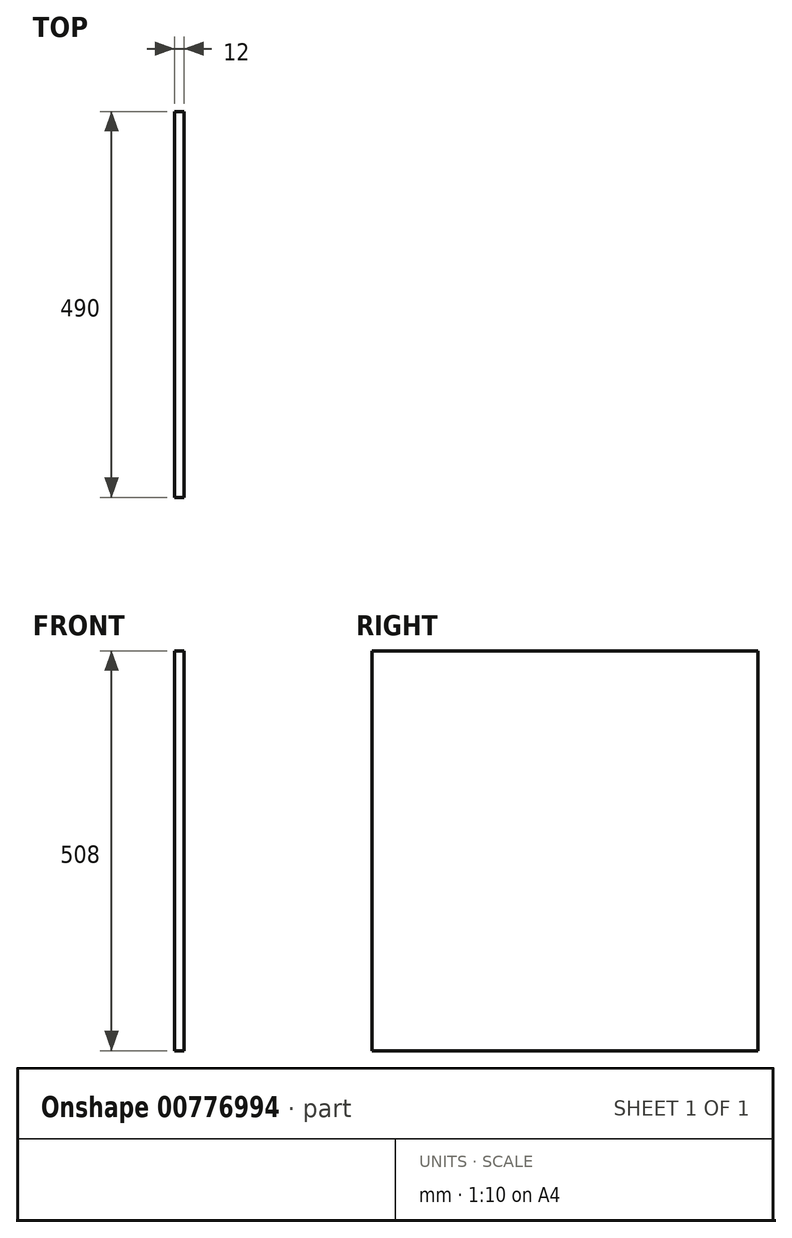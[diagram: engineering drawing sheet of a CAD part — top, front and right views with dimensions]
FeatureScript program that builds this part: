
annotation { "Feature Type Name" : "Feature", "Feature Type Description" : "" }
export const myFeature = defineFeature(function(context is Context, id is Id, definition is map)
    precondition{}
    {
        {
            var Q0;
            Q0=qCreatedBy(makeId("Right.planeOp"),FACE);
            var sketch = newSketch(context, id + "F0", { "sketchPlane" : qUnion([Q0])});
            skLineSegment(sketch, "E0.bottom", {"start": v(-240.04, 384.74) * mm, "end": v(249.96, 384.74) * mm});
            skLineSegment(sketch, "E0.top", {"start": v(-240.04, -123.26) * mm, "end": v(249.96, -123.26) * mm});
            skLineSegment(sketch, "E0.left", {"start": v(-240.04, 384.74) * mm, "end": v(-240.04, -123.26) * mm});
            skLineSegment(sketch, "E0.right", {"start": v(249.96, 384.74) * mm, "end": v(249.96, -123.26) * mm});
            skSolve(sketch);
        }
        {
            var Q0;
            Q0=qSketchRegion(id+"F0",true);
            extrude(context, id + "F1", {"entities" : qUnion([Q0]), "depth" : 12 * mm, "offsetDistance" : 25 * mm});
        }
    });
